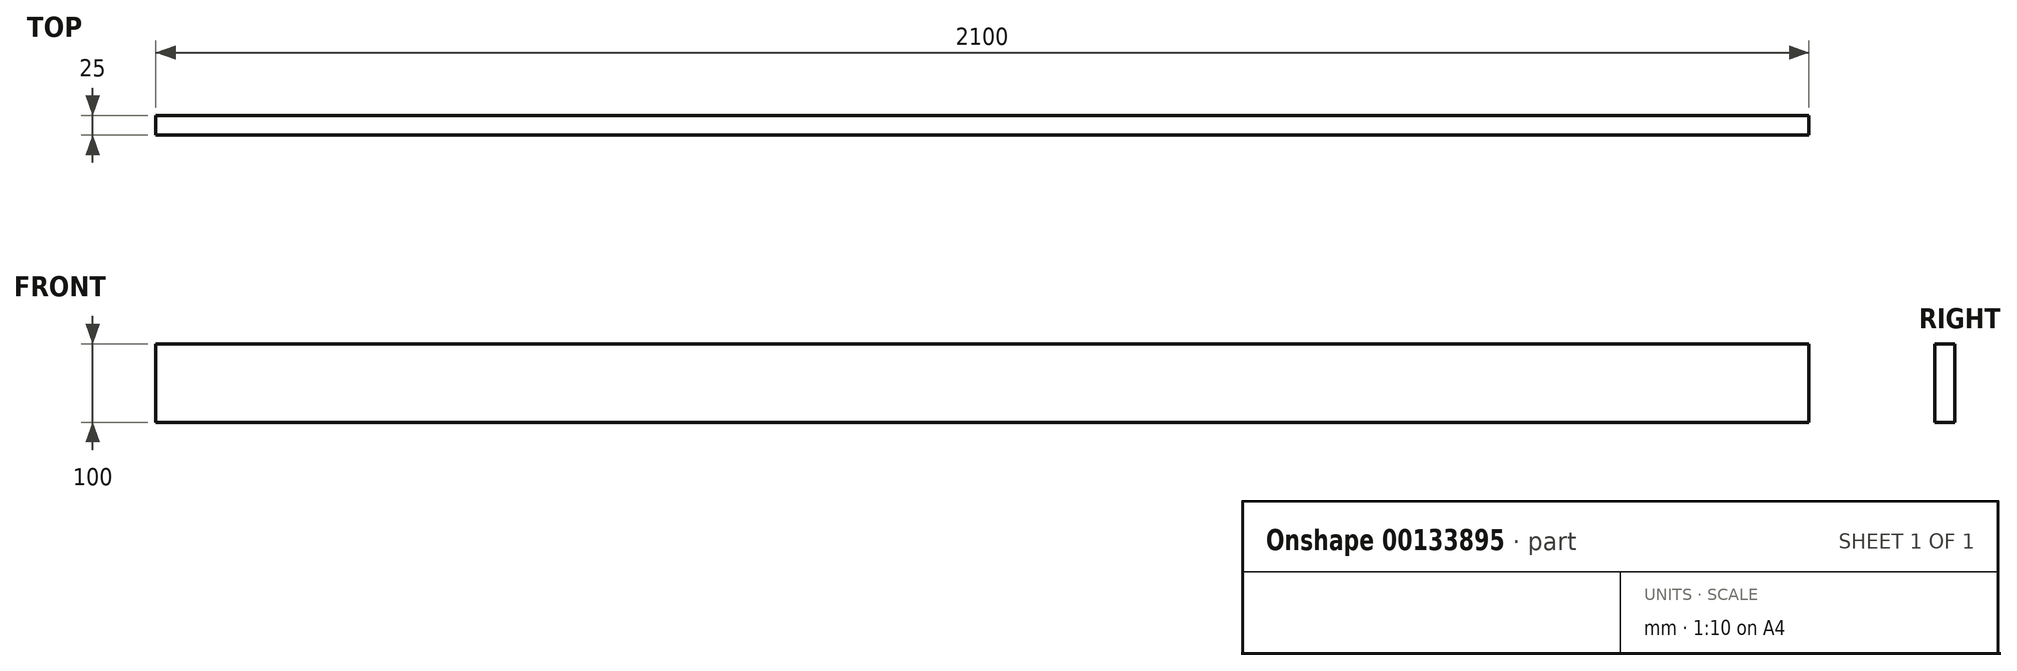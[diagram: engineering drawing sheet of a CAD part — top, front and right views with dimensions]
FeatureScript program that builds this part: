
annotation { "Feature Type Name" : "Feature", "Feature Type Description" : "" }
export const myFeature = defineFeature(function(context is Context, id is Id, definition is map)
    precondition{}
    {
        {
            var Q0;
            Q0=qCreatedBy(makeId("Front.planeOp"),FACE);
            var sketch = newSketch(context, id + "F0", { "sketchPlane" : qUnion([Q0])});
            skLineSegment(sketch, "E0.bottom", {"start": v(1050, -50) * mm, "end": v(-1050, -50) * mm});
            skLineSegment(sketch, "E0.top", {"start": v(1050, 50) * mm, "end": v(-1050, 50) * mm});
            skLineSegment(sketch, "E0.left", {"start": v(1050, -50) * mm, "end": v(1050, 50) * mm});
            skLineSegment(sketch, "E0.right", {"start": v(-1050, -50) * mm, "end": v(-1050, 50) * mm});
            skPoint(sketch, "E0.middle", {"position": v(0, 0) * mm});
            skSolve(sketch);
        }
        {
            var Q0;
            Q0=qSketchRegion(id+"F0",true);
            extrude(context, id + "F1", {"entities" : qUnion([Q0]), "depth" : 25 * mm});
        }
    });
